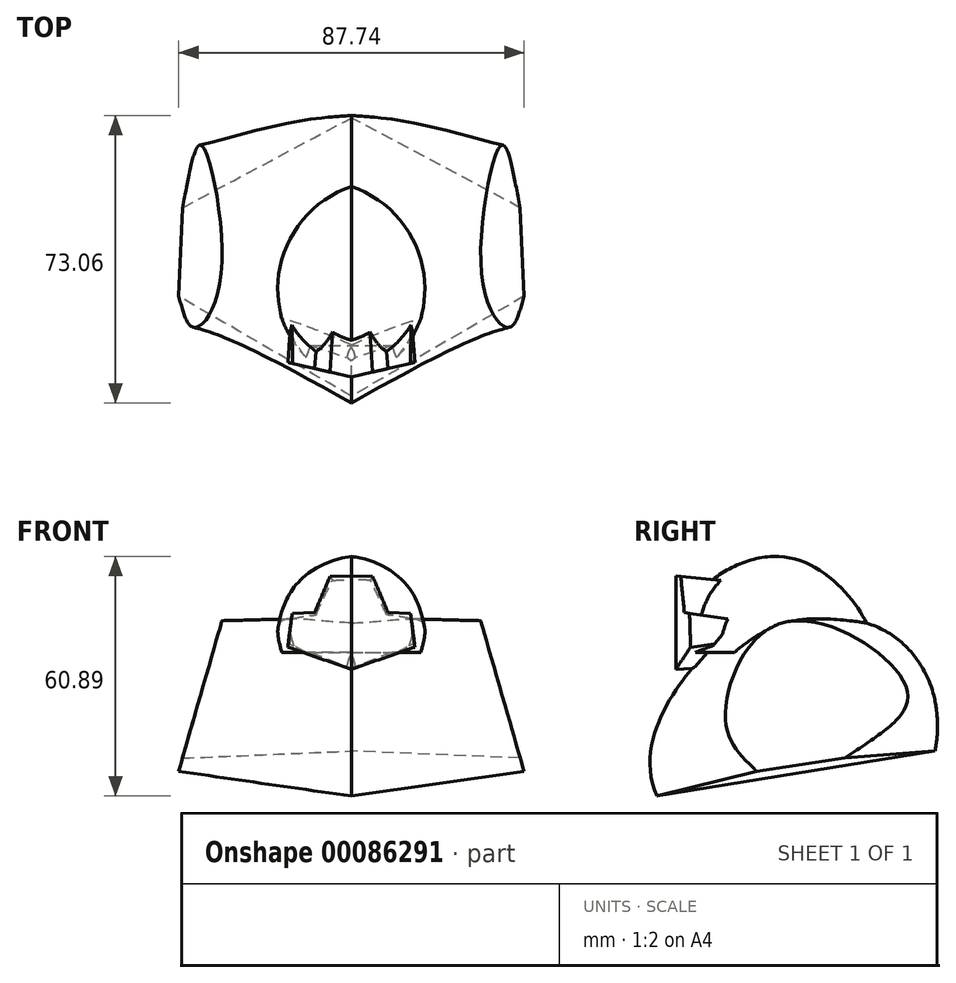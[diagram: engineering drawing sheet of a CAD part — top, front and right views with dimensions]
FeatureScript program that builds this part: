
annotation { "Feature Type Name" : "Feature", "Feature Type Description" : "" }
export const myFeature = defineFeature(function(context is Context, id is Id, definition is map)
    precondition{}
    {
        {
            var Q0;
            Q0=qCreatedBy(makeId("Right.planeOp"),FACE);
            var sketch = newSketch(context, id + "F0", { "sketchPlane" : qUnion([Q0])});
            skFitSpline(sketch, "E0", {"points": [v(-26.94, 0) * mm, v(-16.98, 17.13) * mm, v(4.98, 23.86) * mm, v(22.55, 9.52) * mm, v(26.06, 0) * mm], "startDerivative": vector(27.87, 71.7) * mm, "endDerivative": vector(10.78, -47.5) * mm});
            skLineSegment(sketch, "E1", {"start": v(-26.94, 0) * mm, "end": v(26.06, 0) * mm});
            skSolve(sketch);
        }
        {
            var Q0;
            Q0=qCreatedBy(makeId("Top.planeOp"),FACE);
            var sketch = newSketch(context, id + "F1", { "sketchPlane" : qUnion([Q0])});
            skArc(sketch, "E2", {"start": v(0, -26.94) * mm, "mid": v(19.32, -0.44) * mm, "end": v(0, 26.06) * mm});
            skLineSegment(sketch, "E3", {"start": v(0, -26.94) * mm, "end": v(0, 26.06) * mm});
            skSolve(sketch);
        }
        {
            var Q0;
            Q0=qCreatedBy(makeId("Front.planeOp"),FACE);
            var sketch = newSketch(context, id + "F2", { "sketchPlane" : qUnion([Q0])});
            skFitSpline(sketch, "E4", {"points": [v(0, 24.36) * mm, v(15.35, 15.4) * mm, v(19.32, 0) * mm], "startDerivative": vector(36.2, -4.48) * mm, "endDerivative": vector(1.82, -27.4) * mm});
            skSolve(sketch);
        }
        {
            var Q0;
            Q0=makeQuery(id+"F0.imprint","IMPRINT",FACE,{"disambiguationData":[TD([[makeQuery(id+"F0.imprint","IMPRINT",EDGE,{"derivedFrom":sQuery(id+"F0.wireOp",EDGE,"E0")}),-1.0]])]});
            var Q1;
            Q1=makeQuery(id+"F1.imprint","IMPRINT",FACE,{"disambiguationData":[TD([[makeQuery(id+"F1.imprint","IMPRINT",EDGE,{"derivedFrom":sQuery(id+"F1.wireOp",EDGE,"E2")}),1.0]])]});
            var Q2;
            Q2=sQuery(id+"F0.wireOp",EDGE,"E0");
            var Q3;
            Q3=sQuery(id+"F1.wireOp",EDGE,"E2");
            var Q4;
            Q4=sQuery(id+"F2.wireOp",EDGE,"E4");
            loft(context, id + "F3", {"addGuides" : true, "sheetProfilesArray" : [{ "sheetProfileEntities" : qUnion([Q0]) }, { "sheetProfileEntities" : qUnion([Q1]) }], "wireProfilesArray" : [{ "wireProfileEntities" : qUnion([Q2]) }, { "wireProfileEntities" : qUnion([Q3]) }], "guidesArray" : [{ "guideEntities" : qUnion([Q4]), "guideDerivativeType" : LoftGuideDerivativeType.DEFAULT, "guideDerivativeMagnitude" : 1 }]});
        }
        {
            var Q0;
            Q0=qCreatedBy(makeId("Front.planeOp"),FACE);
            var sketch = newSketch(context, id + "F4", { "sketchPlane" : qUnion([Q0])});
            skLineSegment(sketch, "E5", {"start": v(-17.17, 20) * mm, "end": v(21.57, 20) * mm, "construction": true});
            skSolve(sketch);
        }
        {
            var Q0;
            Q0=qCreatedBy(makeId("Front.planeOp"),FACE);
            var Q1;
            Q1=sQuery(id+"F4.wireOp",EDGE,"E5");
            cPlane(context, id + "F5", {"entities" : qUnion([Q0, Q1]), "cplaneType" : CPlaneType.LINE_ANGLE, "offset" : 150 * mm, "angle" : 140 * degree, "width" : 150 * mm, "height" : 150 * mm});
        }
        {
            var Q0;
            Q0=qCreatedBy(id+"F5.planeOp",FACE);
            var sketch = newSketch(context, id + "F6", { "sketchPlane" : qUnion([Q0])});
            skLineSegment(sketch, "E6", {"start": v(0, 11.64) * mm, "end": v(4.18, 11.64) * mm});
            skLineSegment(sketch, "E7", {"start": v(4.18, 11.64) * mm, "end": v(8.3, 0) * mm});
            skLineSegment(sketch, "E8", {"start": v(8.3, 0) * mm, "end": v(15.14, 0) * mm});
            skLineSegment(sketch, "E9", {"start": v(15.14, 0) * mm, "end": v(15.7, -8.04) * mm});
            skLineSegment(sketch, "E10", {"start": v(15.7, -8.04) * mm, "end": v(0, -16.1) * mm});
            skLineSegment(sketch, "E11", {"start": v(0, -16.1) * mm, "end": v(0, 11.64) * mm});
            skSolve(sketch);
        }
        {
            var Q0;
            Q0=qCreatedBy(id+"F5.planeOp",FACE);
            var sketch = newSketch(context, id + "F7", { "sketchPlane" : qUnion([Q0])});
            skLineSegment(sketch, "E12", {"start": v(-23.17, -33) * mm, "end": v(23.49, -33) * mm, "construction": true});
            skSolve(sketch);
        }
        {
            var Q0;
            Q0=qCreatedBy(makeId("Front.planeOp"),FACE);
            var Q1;
            Q1=sQuery(id+"F7.wireOp",EDGE,"E12");
            cPlane(context, id + "F8", {"entities" : qUnion([Q0, Q1]), "cplaneType" : CPlaneType.LINE_ANGLE, "offset" : 150 * mm, "angle" : 0 * degree, "width" : 150 * mm, "height" : 150 * mm});
        }
        {
            var Q0;
            Q0=qCreatedBy(id+"F8.planeOp",FACE);
            var sketch = newSketch(context, id + "F9", { "sketchPlane" : qUnion([Q0])});
            skLineSegment(sketch, "E13", {"start": v(0, 20.06) * mm, "end": v(-5.82, 20.06) * mm});
            skLineSegment(sketch, "E14", {"start": v(-5.82, 20.06) * mm, "end": v(-9.96, 11.39) * mm});
            skLineSegment(sketch, "E15", {"start": v(-9.96, 11.39) * mm, "end": v(-14.88, 11.39) * mm});
            skLineSegment(sketch, "E16", {"start": v(-14.88, 11.39) * mm, "end": v(-16.85, 0) * mm});
            skLineSegment(sketch, "E17", {"start": v(-16.85, 0) * mm, "end": v(0, -4.57) * mm});
            skLineSegment(sketch, "E18", {"start": v(0, -4.57) * mm, "end": v(0, 20.06) * mm});
            skSolve(sketch);
        }
        {
            var Q1;
            Q1 = qSketchRegion(id + "F9", true);
            var Q2;
            Q2 = qSketchRegion(id + "F6", true);
            loft(context, id + "F10", {"operationType" : NewBodyOperationType.ADD, "sheetProfilesArray" : [{ "sheetProfileEntities" : qUnion([Q1]) }, { "sheetProfileEntities" : qUnion([Q2]) }]});
        }
        {
            var Q0;
            Q0=qCreatedBy(makeId("Top.planeOp"),FACE);
            var sketch = newSketch(context, id + "F11", { "sketchPlane" : qUnion([Q0])});
            skLineSegment(sketch, "E19", {"start": v(0, -24.78) * mm, "end": v(27.79, -18.33) * mm});
            skLineSegment(sketch, "E20", {"start": v(27.79, -18.33) * mm, "end": v(32.23, -37.47) * mm});
            skLineSegment(sketch, "E21", {"start": v(32.23, -37.47) * mm, "end": v(0, -37.47) * mm});
            skLineSegment(sketch, "E22", {"start": v(0, -37.47) * mm, "end": v(0, -24.78) * mm});
            skSolve(sketch);
        }
        {
            var Q0;
            Q0 = qSketchRegion(id + "F11", true);
            extrude(context, id + "F12", {"entities" : qUnion([Q0]), "operationType" : NewBodyOperationType.REMOVE, "endBound" : BoundingType.THROUGH_ALL, "depth" : 25 * mm, "hasSecondDirection" : true, "secondDirectionBound" : SecondDirectionBoundingType.THROUGH_ALL, "secondDirectionOppositeDirection" : true, "secondDirectionDepth" : 25 * mm});
        }
        {
            var Q0;
            Q0=qCreatedBy(makeId("Right.planeOp"),FACE);
            var sketch = newSketch(context, id + "F13", { "sketchPlane" : qUnion([Q0])});
            skFitSpline(sketch, "E23", {"points": [v(-29.62, -36.52) * mm, v(-22.88, -6.9) * mm, v(-6.45, 5.72) * mm, v(28.45, 5.43) * mm, v(41.06, -25.08) * mm], "startDerivative": vector(-56.04, 129.59) * mm, "endDerivative": vector(-29.1, -142.3) * mm});
            skLineSegment(sketch, "E24", {"start": v(-29.62, -36.52) * mm, "end": v(41.06, -25.08) * mm});
            skSolve(sketch);
        }
        {
            var Q0;
            Q0=qCreatedBy(makeId("Front.planeOp"),FACE);
            var sketch = newSketch(context, id + "F14", { "sketchPlane" : qUnion([Q0])});
            skLineSegment(sketch, "E25", {"start": v(32.26, 10.12) * mm, "end": v(49.57, -50) * mm});
            skSolve(sketch);
        }
        {
            var Q0;
            Q0=qCreatedBy(makeId("Right.planeOp"),FACE);
            var Q1;
            Q1=sQuery(id+"F14.wireOp",EDGE,"E25");
            cPlane(context, id + "F15", {"entities" : qUnion([Q0, Q1]), "cplaneType" : CPlaneType.LINE_ANGLE, "offset" : 150 * mm, "angle" : 0 * degree, "width" : 150 * mm, "height" : 150 * mm});
        }
        {
            var Q0;
            Q0=qCreatedBy(id+"F15.planeOp",FACE);
            var sketch = newSketch(context, id + "F16", { "sketchPlane" : qUnion([Q0])});
            skFitSpline(sketch, "E26", {"points": [v(4.24, -41.18) * mm, v(12.08, -28.27) * mm, v(-2.94, -1.76) * mm, v(-33.96, -19.77) * mm, v(-18.23, -37.69) * mm], "startDerivative": vector(57.43, 61.44) * mm, "endDerivative": vector(106.57, -78.54) * mm});
            skLineSegment(sketch, "E27", {"start": v(4.24, -41.18) * mm, "end": v(-18.23, -37.69) * mm});
            skSolve(sketch);
        }
        {
            var Q0;
            Q0=qCreatedBy(makeId("Right.planeOp"),FACE);
            var sketch = newSketch(context, id + "F17", { "sketchPlane" : qUnion([Q0])});
            skLineSegment(sketch, "E28", {"start": v(-34.94, -15.86) * mm, "end": v(49.31, -15.86) * mm, "construction": true});
            skSolve(sketch);
        }
        {
            var Q0;
            Q0=qCreatedBy(makeId("Top.planeOp"),FACE);
            var Q1;
            Q1=sQuery(id+"F17.wireOp",EDGE,"E28");
            cPlane(context, id + "F18", {"entities" : qUnion([Q0, Q1]), "cplaneType" : CPlaneType.LINE_ANGLE, "offset" : 150 * mm, "angle" : 0 * degree, "width" : 150 * mm, "height" : 150 * mm});
        }
        {
            var Q0;
            Q0=qCreatedBy(id+"F18.planeOp",FACE);
            var sketch = newSketch(context, id + "F19", { "sketchPlane" : qUnion([Q0])});
            skFitSpline(sketch, "E29", {"points": [v(0, -41.57) * mm, v(39.74, -32.43) * mm], "startDerivative": vector(43.8, 0.92) * mm, "endDerivative": vector(53.02, 15.67) * mm});
            skSolve(sketch);
        }
        {
            var Q1;
            Q1 = qSketchRegion(id + "F16", true);
            var Q2;
            Q2 = qSketchRegion(id + "F13", true);
            var Q3;
            Q3 = qConstructionFilter(qBodyType(qCreatedBy(id + "F19" ,EDGE), BodyType.WIRE), ConstructionObject.NO);
            var Q4;
            Q4 = qConstructionFilter(qBodyType(qCreatedBy(id + "F21" ,EDGE), BodyType.WIRE), ConstructionObject.NO);
            loft(context, id + "F20", {"operationType" : NewBodyOperationType.ADD, "addGuides" : true, "sheetProfilesArray" : [{ "sheetProfileEntities" : qUnion([Q1]) }, { "sheetProfileEntities" : qUnion([Q2]) }], "guidesArray" : [{ "guideEntities" : qUnion([Q3]), "guideDerivativeType" : LoftGuideDerivativeType.DEFAULT, "guideDerivativeMagnitude" : 1 }, { "guideEntities" : qUnion([Q4]), "guideDerivativeType" : LoftGuideDerivativeType.DEFAULT, "guideDerivativeMagnitude" : 1 }]});
        }
        {
            var Q0;
            Q0=qCreatedBy(id+"F18.planeOp",FACE);
            var sketch = newSketch(context, id + "F21", { "sketchPlane" : qUnion([Q0])});
            skFitSpline(sketch, "E30", {"points": [v(0, 28.33) * mm, v(39.74, 12.16) * mm], "startDerivative": vector(33.2, -2.4) * mm, "endDerivative": vector(27.93, -26.04) * mm});
            skSolve(sketch);
        }
        {
            var Q0;
            Q0=makeQuery(id+"F3.opLoft","SWEPT_BODY",BODY,{"disambiguationData":[OSD([makeQuery(id+"F0.imprint","IMPRINT",FACE,{"disambiguationData":[TD([[makeQuery(id+"F0.imprint","IMPRINT",EDGE,{"derivedFrom":sQuery(id+"F0.wireOp",EDGE,"E0")}),-1.0]])]}),makeQuery(id+"F1.imprint","IMPRINT",FACE,{"disambiguationData":[TD([[makeQuery(id+"F1.imprint","IMPRINT",EDGE,{"derivedFrom":sQuery(id+"F1.wireOp",EDGE,"E2")}),1.0]])]}),sQuery(id+"F2.wireOp",EDGE,"E4")])]});
            var Q1;
            Q1=qCreatedBy(makeId("Right.planeOp"),FACE);
            mirror(context, id + "F22", {"operationType" : NewBodyOperationType.ADD, "entities" : qUnion([Q0]), "mirrorPlane" : qUnion([Q1])});
        }
    });
